# Revit family: LNC3
name_source: partatom
category: Lighting Fixtures
revit_build: Autodesk Revit Architecture 2012 (Build: 20110309_2315(x64)
units: mm (PartAtom-declared; Revit-internal decimal feet)

## types (7) — shared parameters
Apparent Load = 0 VA
Box = Metal - Hubbell - White
Default Elevation = 48.000"
Description = Midsized LED Wallpack
Glass = Hubbell - White Glass
Lamp = LED Lamp
Manufacturer = Hubbell Outdoor Lighting
Manufacturer Fax = (866)-898-1065
Model = LNC3
URL = http://www.hubbelloutdoor.com
Voltage = 120 V
Wattage Comments = 62-87W
Watts = 87 W
With Diffuser = Yes

## per-type parameters (varying)
| type | Backbox |
| Bronze | Metal - Hubbell - Bronze |
| Black | Metal - Hubbell - Black |
| White | Metal - Hubbell - White |
| Gray | Metal - Hubbell - Gray |
| Platinum | Metal - Hubbell - Platinum |
| Forest Green | Metal - Hubbell - Forest Green |
| Red | Metal - Hubbell - Red |

## geometry (parser evidence)
native form markers: Blend x9, Sweep x3
no freeform markers — native parametric forms only
